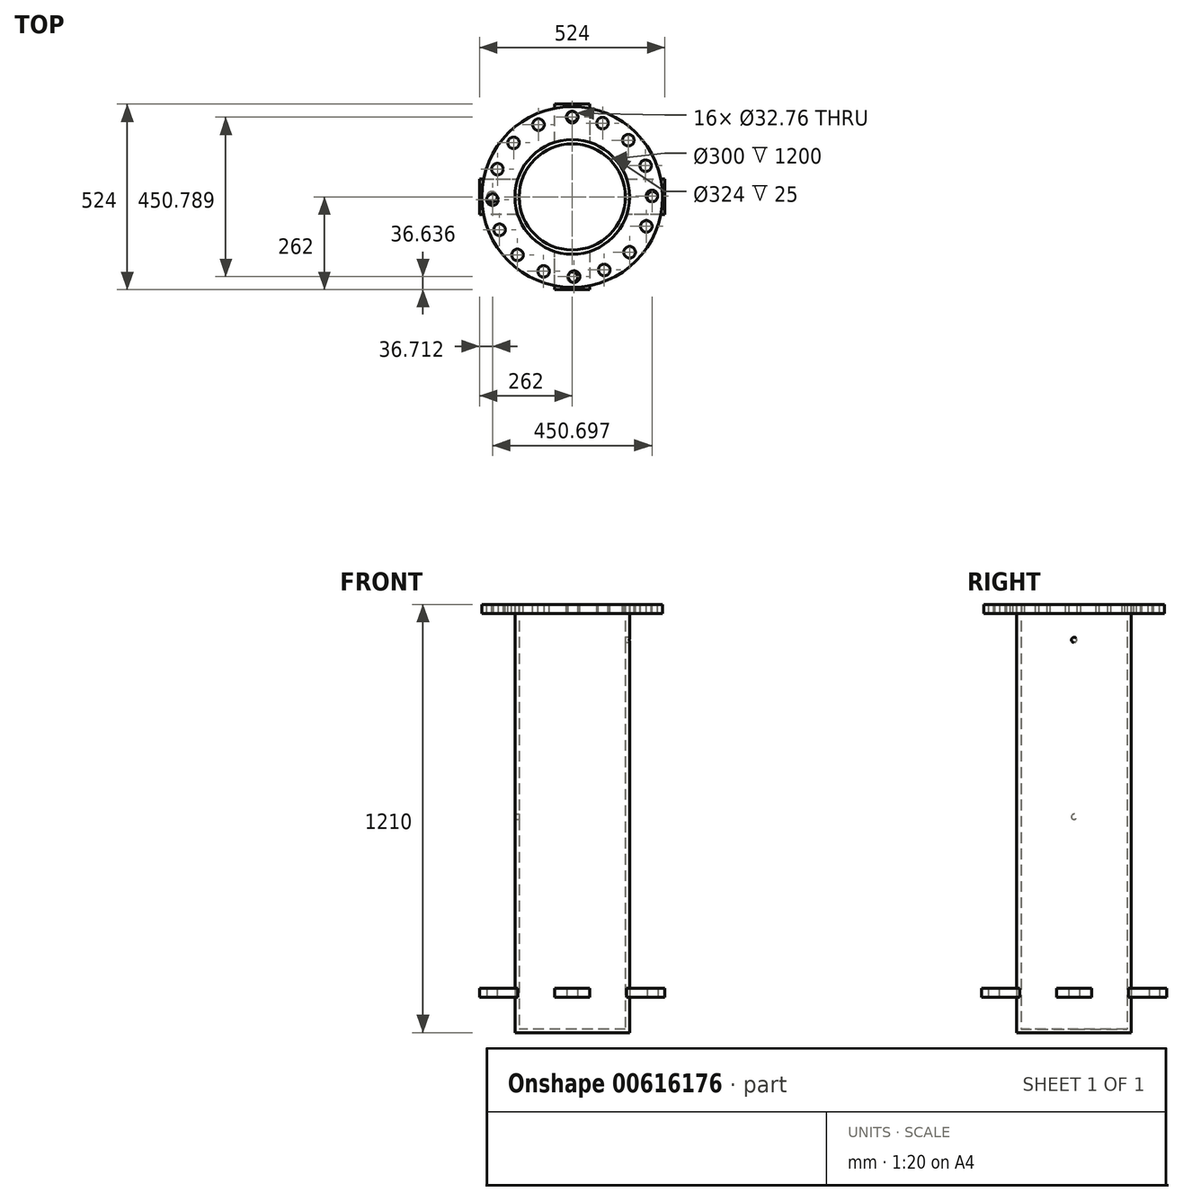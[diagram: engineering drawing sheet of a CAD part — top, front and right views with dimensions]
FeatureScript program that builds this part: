
annotation { "Feature Type Name" : "Feature", "Feature Type Description" : "" }
export const myFeature = defineFeature(function(context is Context, id is Id, definition is map)
    precondition{}
    {
        {
            var Q0;
            Q0=qCreatedBy(makeId("Top.planeOp"),FACE);
            var sketch = newSketch(context, id + "F0", { "sketchPlane" : qUnion([Q0])});
            skCircle(sketch, "E0", {"center": v(0, 0) * mm, "radius": 150 * mm});
            skCircle(sketch, "E1", {"center": v(0, 0) * mm, "radius": 161.95 * mm});
            skSolve(sketch);
        }
        {
            var Q0;
            Q0 = qSketchRegion(id + "F0", true);
            extrude(context, id + "F1", {"entities" : qUnion([Q0]), "depth" : 1200 * mm, "offsetDistance" : 25 * mm});
        }
        {
            var Q0;
            Q0=qCreatedBy(makeId("Top.planeOp"),FACE);
            var sketch = newSketch(context, id + "F2", { "sketchPlane" : qUnion([Q0])});
            skCircle(sketch, "E2", {"center": v(0, 0) * mm, "radius": 161.95 * mm});
            skSolve(sketch);
        }
        {
            var Q0;
            Q0 = qSketchRegion(id + "F2", true);
            extrude(context, id + "F3", {"entities" : qUnion([Q0]), "operationType" : NewBodyOperationType.ADD, "oppositeDirection" : true, "depth" : 10 * mm, "offsetDistance" : 25 * mm});
        }
        {
            var Q0;
            Q0=qCreatedBy(makeId("Right.planeOp"),FACE);
            var sketch = newSketch(context, id + "F4", { "sketchPlane" : qUnion([Q0])});
            skLineSegment(sketch, "E3", {"start": v(0, 0) * mm, "end": v(0, 1100) * mm});
            skCircle(sketch, "E4", {"center": v(0, 1100) * mm, "radius": 7.5 * mm});
            skSolve(sketch);
        }
        {
            var Q0;
            Q0 = qSketchRegion(id + "F4", true);
            extrude(context, id + "F5", {"entities" : qUnion([Q0]), "operationType" : NewBodyOperationType.REMOVE, "depth" : 373 * mm, "offsetDistance" : 25 * mm});
        }
        {
            var Q0;
            Q0=qCreatedBy(makeId("Right.planeOp"),FACE);
            var sketch = newSketch(context, id + "F6", { "sketchPlane" : qUnion([Q0])});
            skLineSegment(sketch, "E5", {"start": v(0, 0) * mm, "end": v(0, 600) * mm});
            skCircle(sketch, "E6", {"center": v(0, 600) * mm, "radius": 7.5 * mm});
            skSolve(sketch);
        }
        {
            var Q0;
            Q0 = qSketchRegion(id + "F6", true);
            extrude(context, id + "F7", {"entities" : qUnion([Q0]), "operationType" : NewBodyOperationType.REMOVE, "oppositeDirection" : true, "depth" : 426 * mm, "offsetDistance" : 25 * mm});
        }
        {
            var Q0;
            Q0=makeQuery(id+"F3.opExtrude","CAP_FACE",FACE,{"disambiguationData":[OSD([sQuery(id+"F2.wireOp",EDGE,"E2")])],"isStart":true});
            cPlane(context, id + "F8", {"entities" : qUnion([Q0]), "cplaneType" : CPlaneType.OFFSET, "offset" : 1200 * mm, "width" : 150 * mm, "height" : 150 * mm});
        }
        {
            var Q0;
            Q0=qCreatedBy(id+"F8.planeOp",FACE);
            var sketch = newSketch(context, id + "F9", { "sketchPlane" : qUnion([Q0])});
            skCircle(sketch, "E7", {"center": v(0, 0) * mm, "radius": 255.52 * mm});
            skCircle(sketch, "E8", {"center": v(0, 0) * mm, "radius": 162 * mm});
            skCircle(sketch, "E9", {"center": v(0, 0) * mm, "radius": 225.43 * mm});
            skCircle(sketch, "E10", {"center": v(0, 225.43) * mm, "radius": 16.38 * mm});
            skCircle(sketch, "E11.1.0", {"center": v(85.66, 208.52) * mm, "radius": 16.38 * mm});
            skCircle(sketch, "E11.2.0", {"center": v(158.47, 160.32) * mm, "radius": 16.38 * mm});
            skCircle(sketch, "E11.3.0", {"center": v(207.5, 88.08) * mm, "radius": 16.38 * mm});
            skCircle(sketch, "E11.4.0", {"center": v(225.4, 2.62) * mm, "radius": 16.38 * mm});
            skCircle(sketch, "E11.5.0", {"center": v(209.5, -83.23) * mm, "radius": 16.38 * mm});
            skCircle(sketch, "E11.6.0", {"center": v(162.16, -156.6) * mm, "radius": 16.38 * mm});
            skCircle(sketch, "E11.7.0", {"center": v(90.49, -206.47) * mm, "radius": 16.38 * mm});
            skCircle(sketch, "E11.8.0", {"center": v(5.25, -225.36) * mm, "radius": 16.38 * mm});
            skCircle(sketch, "E11.9.0", {"center": v(-80.79, -210.45) * mm, "radius": 16.38 * mm});
            skCircle(sketch, "E11.10.0", {"center": v(-154.7, -163.97) * mm, "radius": 16.38 * mm});
            skCircle(sketch, "E11.11.0", {"center": v(-205.4, -92.89) * mm, "radius": 16.38 * mm});
            skCircle(sketch, "E11.12.0", {"center": v(-225.29, -7.87) * mm, "radius": 16.38 * mm});
            skCircle(sketch, "E11.13.0", {"center": v(-211.38, 78.33) * mm, "radius": 16.38 * mm});
            skCircle(sketch, "E11.14.0", {"center": v(-165.76, 152.78) * mm, "radius": 16.38 * mm});
            skCircle(sketch, "E11.15.0", {"center": v(-95.27, 204.3) * mm, "radius": 16.38 * mm});
            skLineSegment(sketch, "E11.anchor1", {"start": v(0, 0) * mm, "end": v(0, 225.43) * mm, "construction": true});
            skLineSegment(sketch, "E11.anchor2", {"start": v(0, 0) * mm, "end": v(-95.27, 204.3) * mm, "construction": true});
            skSolve(sketch);
        }
        {
            var Q0;
            Q0 = qSketchRegion(id + "F9", true);
            var Q1;
            Q1=makeQuery(id+"F9.imprint","IMPRINT",FACE,{"disambiguationData":[TD([[makeQuery(id+"F9.imprint","IMPRINT",EDGE,{"derivedFrom":sQuery(id+"F9.wireOp",EDGE,"E8")}),-1.0]])]});
            extrude(context, id + "F10", {"entities" : qUnion([Q0, Q1]), "oppositeDirection" : true, "depth" : 25 * mm, "offsetDistance" : 25 * mm});
        }
        {
            var Q0;
            Q0=makeQuery(id+"F3.opExtrude","CAP_FACE",FACE,{"disambiguationData":[OSD([sQuery(id+"F2.wireOp",EDGE,"E2")])],"isStart":false});
            var sketch = newSketch(context, id + "F11", { "sketchPlane" : qUnion([Q0])});
            skLineSegment(sketch, "E12", {"start": v(0, 0) * mm, "end": v(0, 162) * mm});
            skArc(sketch, "E13", {"start": v(50, 154.1) * mm, "mid": v(0, 162) * mm, "end": v(-50, 154.1) * mm});
            skLineSegment(sketch, "E14", {"start": v(0, 162) * mm, "end": v(0, 262) * mm});
            skLineSegment(sketch, "E15", {"start": v(0, 262) * mm, "end": v(50, 262) * mm});
            skLineSegment(sketch, "E16", {"start": v(0, 262) * mm, "end": v(-50, 262) * mm});
            skLineSegment(sketch, "E17", {"start": v(-50, 262) * mm, "end": v(-50, 154.1) * mm});
            skLineSegment(sketch, "E18", {"start": v(50, 154.1) * mm, "end": v(50, 262) * mm});
            skPoint(sketch, "E19.orphan", {"position": v(-50, 145.15) * mm});
            skPoint(sketch, "E20.orphan", {"position": v(50, 145.15) * mm});
            skLineSegment(sketch, "E21", {"start": v(0, 162) * mm, "end": v(0, 227) * mm});
            skCircle(sketch, "E22", {"center": v(0, 227) * mm, "radius": 15 * mm});
            skSolve(sketch);
        }
        {
            var Q0;
            Q0 = qSketchRegion(id + "F11", true);
            extrude(context, id + "F12", {"entities" : qUnion([Q0]), "oppositeDirection" : true, "depth" : 25 * mm, "offsetDistance" : 25 * mm});
        }
        {
            var Q0;
            Q0=makeQuery(id+"F12.opExtrude","SWEPT_BODY",BODY,{"disambiguationData":[OSD([sQuery(id+"F11.wireOp",EDGE,"E13"),sQuery(id+"F11.wireOp",EDGE,"E15"),sQuery(id+"F11.wireOp",EDGE,"E16"),sQuery(id+"F11.wireOp",EDGE,"E17"),sQuery(id+"F11.wireOp",EDGE,"E18"),sQuery(id+"F11.wireOp",EDGE,"E22")])]});
            var Q1;
            Q1=makeQuery(id+"F12.opExtrude","SWEPT_EDGE",EDGE,{"disambiguationData":[OSD([sQuery(id+"F11.wireOp",EDGE,"E16"),sQuery(id+"F11.wireOp",EDGE,"E17")])]});
            var Q2;
            Q2=makeQuery(id+"F12.opExtrude","SWEPT_EDGE",EDGE,{"disambiguationData":[OSD([sQuery(id+"F11.wireOp",EDGE,"E15"),sQuery(id+"F11.wireOp",EDGE,"E18")])]});
            transform(context, id + "F13", {"entities" : qUnion([Q0]), "transformType" : TransformType.TRANSLATION_DISTANCE, "transformDirection" : qUnion([Q2]), "distance" : 100 * mm, "oppositeDirection" : true, "makeCopy" : false});
        }
        {
            var Q0;
            Q0=makeQuery(id+"F12.opExtrude","SWEPT_BODY",BODY,{"disambiguationData":[OSD([sQuery(id+"F11.wireOp",EDGE,"E13"),sQuery(id+"F11.wireOp",EDGE,"E15"),sQuery(id+"F11.wireOp",EDGE,"E16"),sQuery(id+"F11.wireOp",EDGE,"E17"),sQuery(id+"F11.wireOp",EDGE,"E18"),sQuery(id+"F11.wireOp",EDGE,"E22")])]});
            var Q1;
            Q1=makeQuery(id+"F3.opExtrude","CAP_EDGE",EDGE,{"disambiguationData":[OSD([sQuery(id+"F2.wireOp",EDGE,"E2")])],"isStart":false});
            circularPattern(context, id + "F14", {"entities" : qUnion([Q0]), "axis" : qUnion([Q1]), "angle" : 360 * degree, "instanceCount" : 4, "equalSpace" : true});
        }
    });
